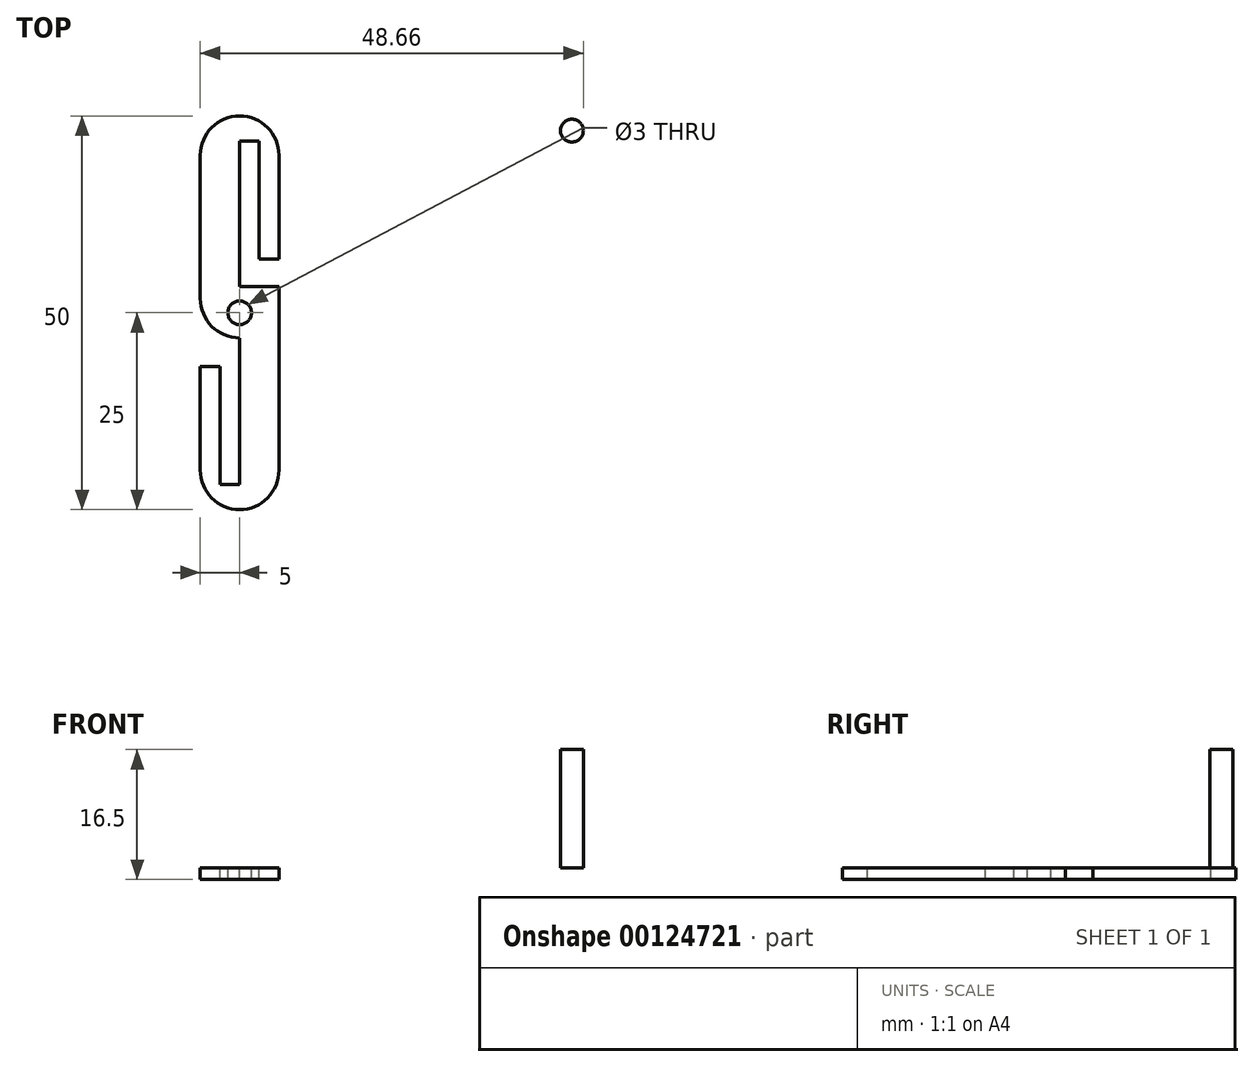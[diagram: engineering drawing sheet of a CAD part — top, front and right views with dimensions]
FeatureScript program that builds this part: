
annotation { "Feature Type Name" : "Feature", "Feature Type Description" : "" }
export const myFeature = defineFeature(function(context is Context, id is Id, definition is map)
    precondition{}
    {
        {
            var Q0;
            Q0=qCreatedBy(makeId("Top.planeOp"),FACE);
            var sketch = newSketch(context, id + "F0", { "sketchPlane" : qUnion([Q0])});
            skLineSegment(sketch, "E0.bottom", {"start": v(5, -25) * mm, "end": v(-5, -25) * mm});
            skLineSegment(sketch, "E0.top", {"start": v(5, 25) * mm, "end": v(-5, 25) * mm});
            skLineSegment(sketch, "E0.left", {"start": v(5, -25) * mm, "end": v(5, 25) * mm});
            skLineSegment(sketch, "E0.right", {"start": v(-5, -25) * mm, "end": v(-5, 25) * mm});
            skPoint(sketch, "E0.middle", {"position": v(0, 0) * mm});
            skLineSegment(sketch, "E1", {"start": v(-5, 0) * mm, "end": v(5, 0) * mm, "construction": true});
            skLineSegment(sketch, "E2", {"start": v(-5, -6.8) * mm, "end": v(-2.5, -6.8) * mm});
            skLineSegment(sketch, "E3", {"start": v(-2.5, -6.8) * mm, "end": v(-2.5, -21.8) * mm});
            skLineSegment(sketch, "E4", {"start": v(0.54, 0) * mm, "end": v(-5, 0) * mm});
            skLineSegment(sketch, "E5", {"start": v(-2.5, -21.8) * mm, "end": v(0, -21.8) * mm});
            skLineSegment(sketch, "E6", {"start": v(0, -21.8) * mm, "end": v(0, 0) * mm});
            skLineSegment(sketch, "E7", {"start": v(0, 21.8) * mm, "end": v(2.5, 21.8) * mm});
            skLineSegment(sketch, "E8", {"start": v(2.5, 21.8) * mm, "end": v(2.5, 6.8) * mm});
            skLineSegment(sketch, "E9", {"start": v(2.5, 6.8) * mm, "end": v(5, 6.8) * mm});
            skLineSegment(sketch, "E10", {"start": v(0, 21.8) * mm, "end": v(0, 0) * mm});
            skLineSegment(sketch, "E11", {"start": v(0, 0) * mm, "end": v(5, 0) * mm});
            skLineSegment(sketch, "E12", {"start": v(-5, 3.32) * mm, "end": v(5, 3.32) * mm});
            skLineSegment(sketch, "E13", {"start": v(-5, -3.18) * mm, "end": v(5, -3.18) * mm});
            skCircle(sketch, "E14", {"center": v(42.2, 23.14) * mm, "radius": 1.45 * mm});
            skCircle(sketch, "E15", {"center": v(0, 0) * mm, "radius": 1.5 * mm});
            skSolve(sketch);
        }
        {
            var Q0;
            {var subQ1=sQuery(id+"F0.wireOp",EDGE,"E0.top");Q0=makeQuery(id+"F0.imprint","IMPRINT",FACE,{"disambiguationData":[TD([[makeQuery(id+"F0.imprint","IMPRINT",EDGE,{"derivedFrom":subQ1}),1.0]])]});}
            var Q1;
            {var subQ6=sQuery(id+"F0.wireOp",EDGE,"E0.bottom");Q1=makeQuery(id+"F0.imprint","IMPRINT",FACE,{"disambiguationData":[TD([[makeQuery(id+"F0.imprint","IMPRINT",EDGE,{"derivedFrom":subQ6}),-1.0]])]});}
            var Q2;
            {var subQ1=sQuery(id+"F0.wireOp",EDGE,"E0.left");var subQ5=sQuery(id+"F0.wireOp",EDGE,"E11");var subQ6=makeQuery(id+"F0.imprint","INTERSECT",VERTEX,{"derivedFrom":[subQ1,subQ5]});Q2=makeQuery(id+"F0.imprint","IMPRINT",FACE,{"disambiguationData":[TD([[makeQuery(id+"F0.imprint","IMPRINT",EDGE,{"disambiguationData":[TD([[subQ6,-1.0]])],"derivedFrom":subQ1}),1.0]])]});}
            var Q3;
            {var subQ1=sQuery(id+"F0.wireOp",EDGE,"E0.right");var subQ5=sQuery(id+"F0.wireOp",EDGE,"E4");var subQ6=makeQuery(id+"F0.imprint","INTERSECT",VERTEX,{"derivedFrom":[subQ1,subQ5]});Q3=makeQuery(id+"F0.imprint","IMPRINT",FACE,{"disambiguationData":[TD([[makeQuery(id+"F0.imprint","IMPRINT",EDGE,{"disambiguationData":[TD([[subQ6,-1.0]])],"derivedFrom":subQ1}),-1.0]])]});}
            var Q4;
            {var subQ1=sQuery(id+"F0.wireOp",EDGE,"E0.right");var subQ7=sQuery(id+"F0.wireOp",EDGE,"E4");var subQ8=makeQuery(id+"F0.imprint","INTERSECT",VERTEX,{"derivedFrom":[subQ1,subQ7]});Q4=makeQuery(id+"F0.imprint","IMPRINT",FACE,{"disambiguationData":[TD([[makeQuery(id+"F0.imprint","IMPRINT",EDGE,{"disambiguationData":[TD([[subQ8,1.0]])],"derivedFrom":subQ1}),-1.0]])]});}
            var Q5;
            {var subQ0=sQuery(id+"F0.wireOp",EDGE,"E11");var subQ1=sQuery(id+"F0.wireOp",EDGE,"E0.left");var subQ2=makeQuery(id+"F0.imprint","INTERSECT",VERTEX,{"derivedFrom":[subQ1,subQ0]});Q5=makeQuery(id+"F0.imprint","IMPRINT",FACE,{"disambiguationData":[TD([[makeQuery(id+"F0.imprint","IMPRINT",EDGE,{"disambiguationData":[TD([[subQ2,1.0]])],"derivedFrom":subQ1}),1.0]])]});}
            extrude(context, id + "F1", {"entities" : qUnion([Q0, Q1, Q2, Q3, Q4, Q5]), "oppositeDirection" : true, "depth" : 1.5 * mm});
        }
        {
            var Q0;
            Q0=makeQuery(id+"F1.opExtrude","SWEPT_EDGE",EDGE,{"disambiguationData":[OSD([sQuery(id+"F0.wireOp",EDGE,"E0.top"),sQuery(id+"F0.wireOp",EDGE,"E0.left")])]});
            var Q1;
            Q1=makeQuery(id+"F1.opExtrude","SWEPT_EDGE",EDGE,{"disambiguationData":[OSD([sQuery(id+"F0.wireOp",EDGE,"E0.top"),sQuery(id+"F0.wireOp",EDGE,"E0.right")])]});
            var Q2;
            Q2=makeQuery(id+"F1.opExtrude","SWEPT_EDGE",EDGE,{"disambiguationData":[OSD([sQuery(id+"F0.wireOp",EDGE,"E0.right"),sQuery(id+"F0.wireOp",EDGE,"E13")])]});
            var Q3;
            Q3=makeQuery(id+"F1.opExtrude","SWEPT_EDGE",EDGE,{"disambiguationData":[OSD([sQuery(id+"F0.wireOp",EDGE,"E0.bottom"),sQuery(id+"F0.wireOp",EDGE,"E0.left")])]});
            var Q4;
            Q4=makeQuery(id+"F1.opExtrude","SWEPT_EDGE",EDGE,{"disambiguationData":[OSD([sQuery(id+"F0.wireOp",EDGE,"E0.bottom"),sQuery(id+"F0.wireOp",EDGE,"E0.right")])]});
            fillet(context, id + "F2", {"entities" : qUnion([Q0, Q1, Q2, Q3, Q4]), "radius" : 5 * mm, "tangentPropagation" : true, "allowEdgeOverflow" : false});
        }
        {
            var Q0;
            Q0=makeQuery(id+"F0.imprint","IMPRINT",FACE,{"disambiguationData":[TD([[makeQuery(id+"F0.imprint","IMPRINT",EDGE,{"derivedFrom":sQuery(id+"F0.wireOp",EDGE,"E14")}),1.0]])]});
            extrude(context, id + "F3", {"entities" : qUnion([Q0]), "depth" : 15 * mm});
        }
    });
